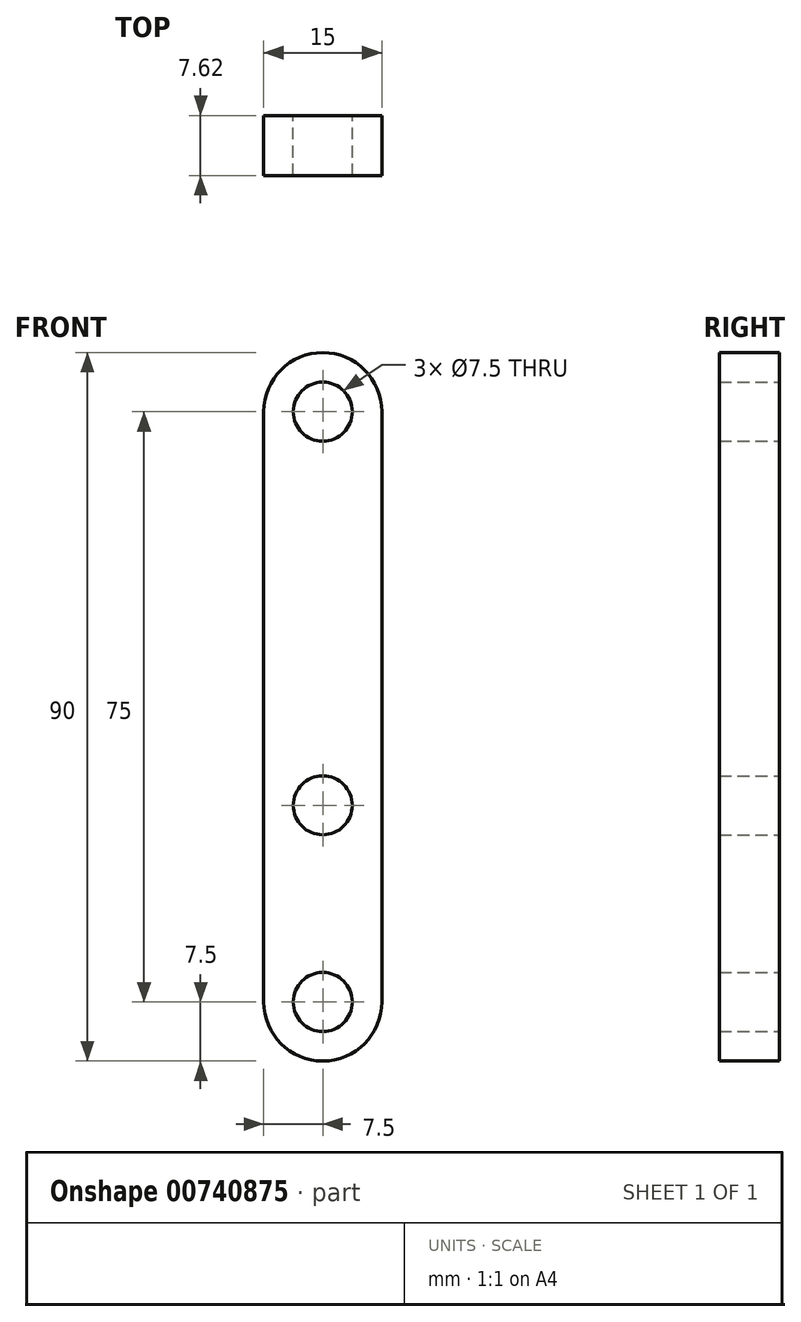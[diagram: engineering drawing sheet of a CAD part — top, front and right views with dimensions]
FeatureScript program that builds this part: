
annotation { "Feature Type Name" : "Feature", "Feature Type Description" : "" }
export const myFeature = defineFeature(function(context is Context, id is Id, definition is map)
    precondition{}
    {
        {
            var Q0;
            Q0=qCreatedBy(makeId("Front.planeOp"),FACE);
            var sketch = newSketch(context, id + "F0", { "sketchPlane" : qUnion([Q0])});
            skCircle(sketch, "E0", {"center": v(0, 0) * mm, "radius": 3.75 * mm});
            skCircle(sketch, "E1", {"center": v(0, 50) * mm, "radius": 3.75 * mm});
            skCircle(sketch, "E2", {"center": v(0, -25) * mm, "radius": 3.75 * mm});
            skCircle(sketch, "E3", {"center": v(0, -25) * mm, "radius": 7.5 * mm});
            skCircle(sketch, "E4", {"center": v(0, 50) * mm, "radius": 7.5 * mm});
            skLineSegment(sketch, "E5", {"start": v(-7.5, -25) * mm, "end": v(-7.5, 50) * mm});
            skLineSegment(sketch, "E6", {"start": v(7.5, 50) * mm, "end": v(7.5, -25) * mm});
            skSolve(sketch);
        }
        {
            var Q0;
            Q0 = qSketchRegion(id + "F0", true);
            extrude(context, id + "F1", {"entities" : qUnion([Q0]), "depth" : 7.62 * mm, "offsetDistance" : 25.4 * mm});
        }
    });
